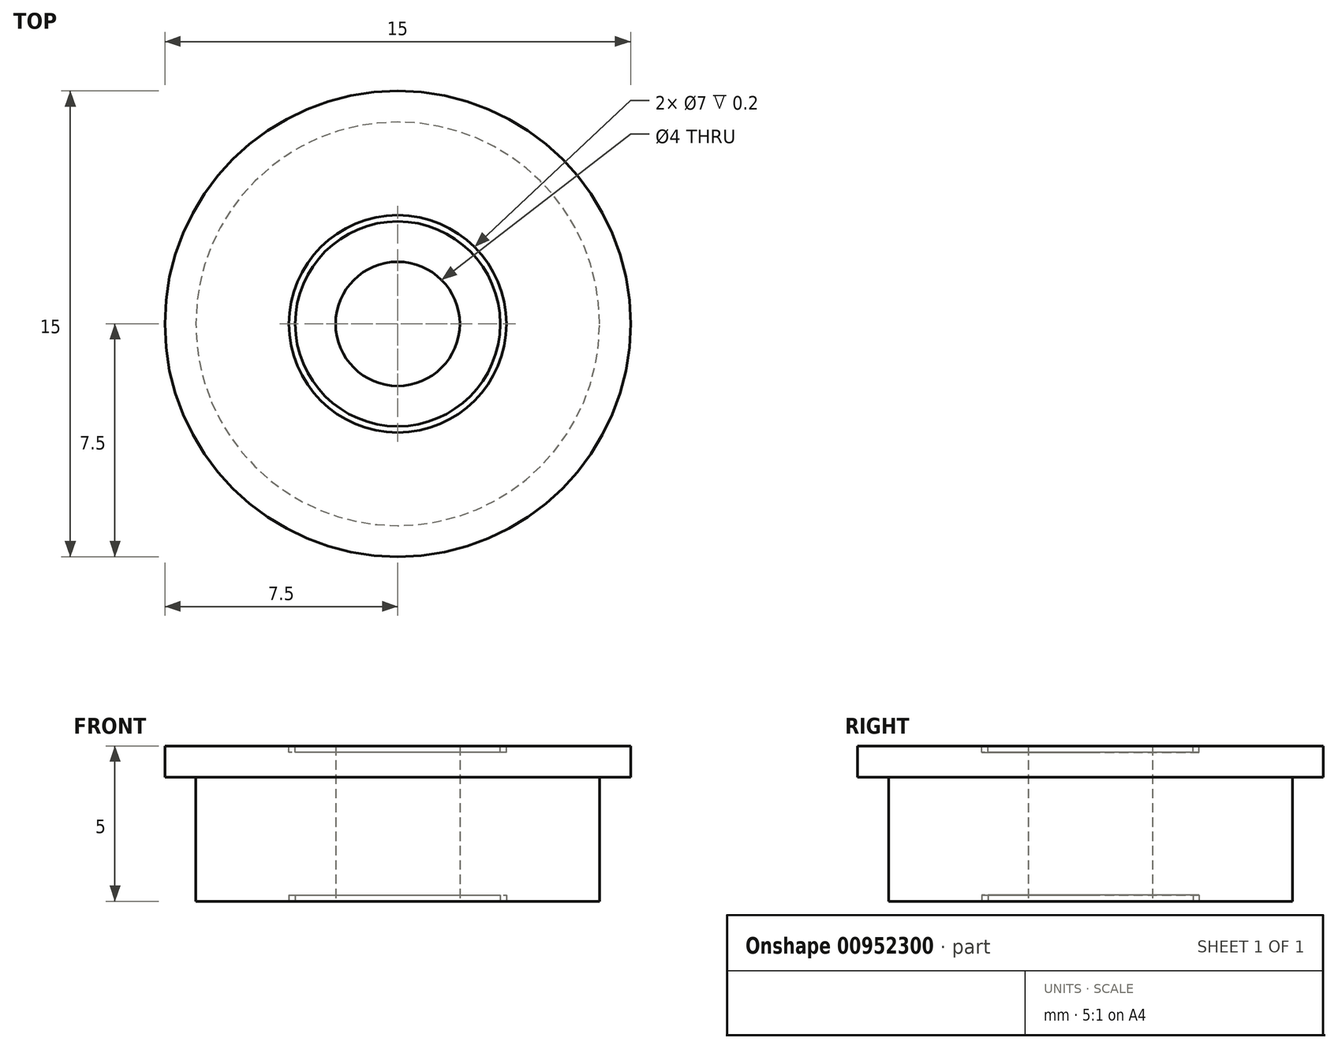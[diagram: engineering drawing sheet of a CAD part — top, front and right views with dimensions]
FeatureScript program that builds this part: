
annotation { "Feature Type Name" : "Feature", "Feature Type Description" : "" }
export const myFeature = defineFeature(function(context is Context, id is Id, definition is map)
    precondition{}
    {
        {
            var Q0;
            Q0=qCreatedBy(makeId("Top.planeOp"),FACE);
            var sketch = newSketch(context, id + "F0", { "sketchPlane" : qUnion([Q0])});
            skCircle(sketch, "E0", {"center": v(0, 0) * mm, "radius": 2 * mm});
            skCircle(sketch, "E1", {"center": v(0, 0) * mm, "radius": 6.5 * mm});
            skSolve(sketch);
        }
        {
            var Q0;
            Q0 = qSketchRegion(id + "F0", true);
            extrude(context, id + "F1", {"entities" : qUnion([Q0]), "depth" : 5 * mm, "offsetDistance" : 25 * mm});
        }
        {
            var Q0;
            Q0=makeQuery(id+"F1.opExtrude","CAP_FACE",FACE,{"disambiguationData":[OSD([sQuery(id+"F0.wireOp",EDGE,"E0"),sQuery(id+"F0.wireOp",EDGE,"E1")])],"isStart":false});
            var sketch = newSketch(context, id + "F2", { "sketchPlane" : qUnion([Q0])});
            skCircle(sketch, "E2", {"center": v(0, 0) * mm, "radius": 7.5 * mm});
            skCircle(sketch, "E3", {"center": v(0, 0) * mm, "radius": 5.1 * mm});
            skSolve(sketch);
        }
        {
            var Q0;
            Q0 = qSketchRegion(id + "F2", true);
            extrude(context, id + "F3", {"entities" : qUnion([Q0]), "operationType" : NewBodyOperationType.ADD, "oppositeDirection" : true, "depth" : 1 * mm, "offsetDistance" : 25 * mm});
        }
        {
            var Q0;
            Q0=makeQuery(id+"F3.boolean.opBoolean","MERGE",FACE,{"derivedFrom":[makeQuery(id+"F1.opExtrude","CAP_FACE",FACE,{"disambiguationData":[OSD([sQuery(id+"F0.wireOp",EDGE,"E0"),sQuery(id+"F0.wireOp",EDGE,"E1")])],"isStart":false}),makeQuery(id+"F3.opExtrude","CAP_FACE",FACE,{"disambiguationData":[OSD([sQuery(id+"F2.wireOp",EDGE,"E2"),sQuery(id+"F2.wireOp",EDGE,"E3")])],"isStart":true})]});
            var sketch = newSketch(context, id + "F4", { "sketchPlane" : qUnion([Q0])});
            skCircle(sketch, "E4", {"center": v(0, 0) * mm, "radius": 3.3 * mm});
            skCircle(sketch, "E5", {"center": v(0, 0) * mm, "radius": 3.5 * mm});
            skSolve(sketch);
        }
        {
            var Q0;
            Q0 = qSketchRegion(id + "F4", true);
            extrude(context, id + "F5", {"entities" : qUnion([Q0]), "operationType" : NewBodyOperationType.REMOVE, "oppositeDirection" : true, "depth" : 0.2 * mm, "offsetDistance" : 25 * mm});
        }
        {
            var Q0;
            Q0=makeQuery(id+"F1.opExtrude","CAP_FACE",FACE,{"disambiguationData":[OSD([sQuery(id+"F0.wireOp",EDGE,"E0"),sQuery(id+"F0.wireOp",EDGE,"E1")])],"isStart":true});
            var sketch = newSketch(context, id + "F6", { "sketchPlane" : qUnion([Q0])});
            skCircle(sketch, "E6", {"center": v(0, 0) * mm, "radius": 3.3 * mm});
            skCircle(sketch, "E7", {"center": v(0, 0) * mm, "radius": 3.5 * mm});
            skSolve(sketch);
        }
        {
            var Q0;
            Q0 = qSketchRegion(id + "F6", true);
            extrude(context, id + "F7", {"entities" : qUnion([Q0]), "operationType" : NewBodyOperationType.REMOVE, "oppositeDirection" : true, "depth" : 0.2 * mm, "offsetDistance" : 25 * mm});
        }
    });
